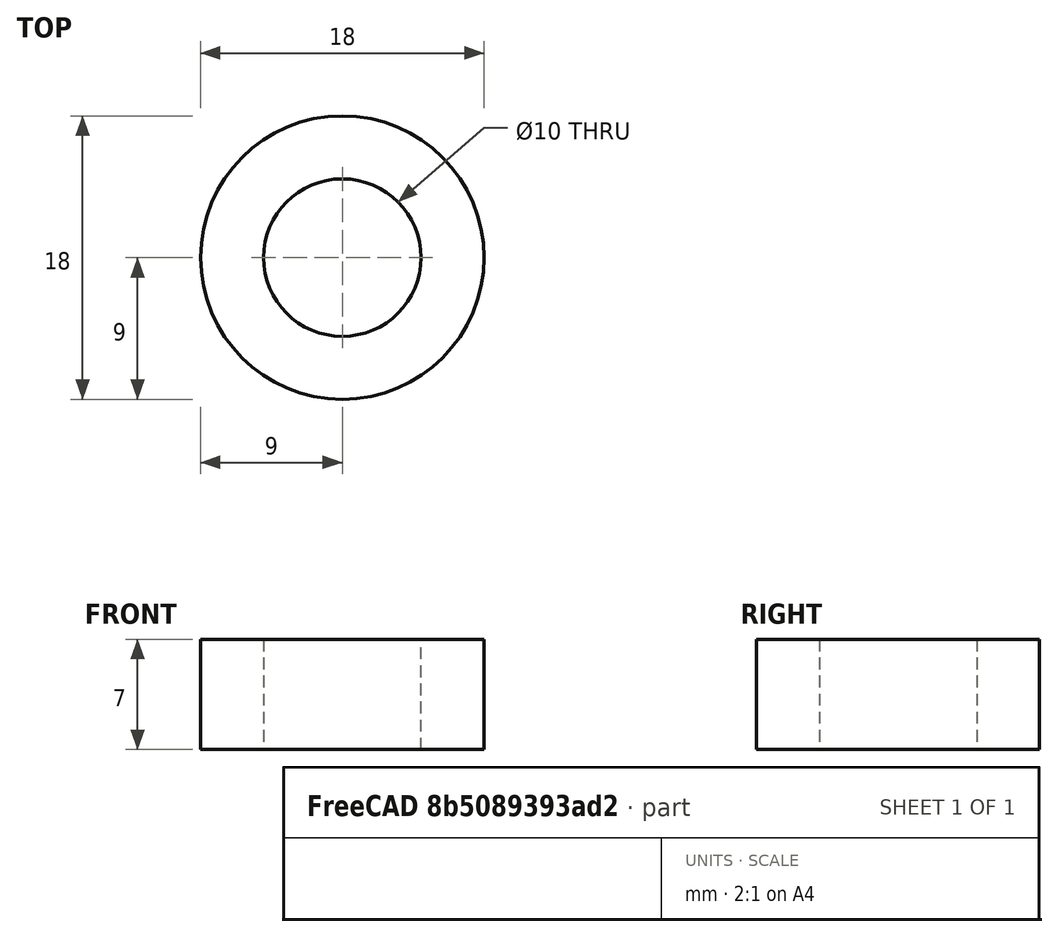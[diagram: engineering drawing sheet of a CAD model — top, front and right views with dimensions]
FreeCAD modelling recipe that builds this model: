
FCSTD DOCUMENT  (FreeCAD 0.19R24276 (Git))
Label: Ring_18x10
License: All rights reserved
LicenseURL: http://en.wikipedia.org/wiki/All_rights_reserved
objects: Sketcher::SketchObject×1, PartDesign::Pad×1, PartDesign::Body×1
note: 4 computed .brp shape members not serialized (recipe doc carries the construction recipe); baked Part::Feature solids carry a one-line shape summary decoded from their .brp

FEATURE [Sketcher::SketchObject] Sketch
  FullyConstrained = true
  MapMode = 5
  Support = -> [XY_Plane]
  sketch-geometry (2):
    g0: Circle CenterX=0 CenterY=0 CenterZ=0 NormalX=0 NormalY=0 NormalZ=1 AngleXU=0 Radius=9
    g1: Circle CenterX=0 CenterY=0 CenterZ=0 NormalX=0 NormalY=0 NormalZ=1 AngleXU=0 Radius=5
  constraints (4):
    c: Coincident(g0,g-1)
    c: Coincident(g1,g0)
    c: Diameter(g0) = 18
    c: Diameter(g1) = 10
FEATURE [PartDesign::Pad] Pad
  Direction = (1,1,1)
  Length = 7
  Length2 = 100
  Profile = -> Sketch
  Type = 0
FEATURE [PartDesign::Body] Body
  Group = -> [Sketch,Pad]
  Origin = -> Origin
  Tip = -> Pad
